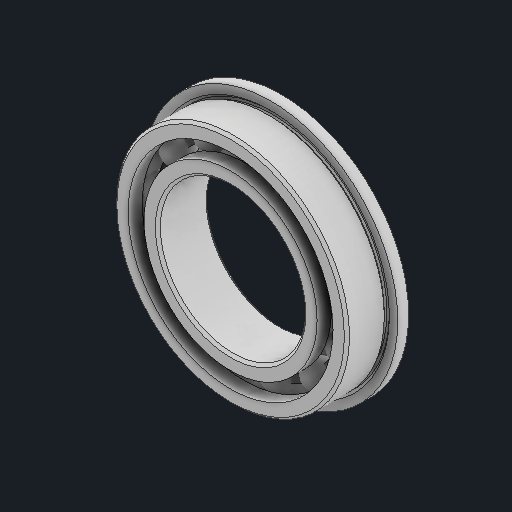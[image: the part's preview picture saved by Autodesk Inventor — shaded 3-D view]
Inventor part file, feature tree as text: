
AUTODESK INVENTOR PART (.ipt)
format: ipt  version: 2024 (Build 280153000, 153)  size: 673,280 bytes
history: native  units: in
note: dims shown in document units (in); Inventor stores cm internally (conversion verified against a paired STEP export)
features: other x12, revolve x4
ambient origin geometry x8: Origin, YZ Plane, XZ Plane, XY Plane, X Axis, Y Axis, Z Axis, Center Point
bodies: Solid1 (feature_tree), Solid2 (feature_tree), Solid3 (feature_tree), Solid4 (feature_tree), Solid5 (feature_tree), Solid6 (feature_tree), Solid7 (feature_tree), Solid8 (feature_tree), Solid9 (feature_tree), Solid10 (feature_tree), Solid11 (feature_tree), Solid12 (feature_tree), Solid13 (feature_tree), Solid14 (feature_tree), Solid15 (feature_tree), Solid16 (feature_tree)
feature tree (16):
  revolve  "Revolve1"  [1 undecoded]
  revolve  "Revolve3"  [1 undecoded]
  revolve  "Revolve4"  [1 undecoded]
  other  "CirPattern1[1]"
  other  "CirPattern1[2]"
  other  "CirPattern1[3]"
  other  "CirPattern1[4]"
  other  "CirPattern1[5]"
  other  "CirPattern1[6]"
  other  "CirPattern1[7]"
  other  "CirPattern1[8]"
  other  "CirPattern1[9]"
  other  "CirPattern1[10]"
  other  "CirPattern1[11]"
  other  "CirPattern1[12]"
  revolve  "Revolve6"  [1 undecoded]
note: 4 required parameter values undecoded (feature->parameter linkage not recoverable at this tier; creation-order binding heuristic only, values carry confidence <= 0.55)
